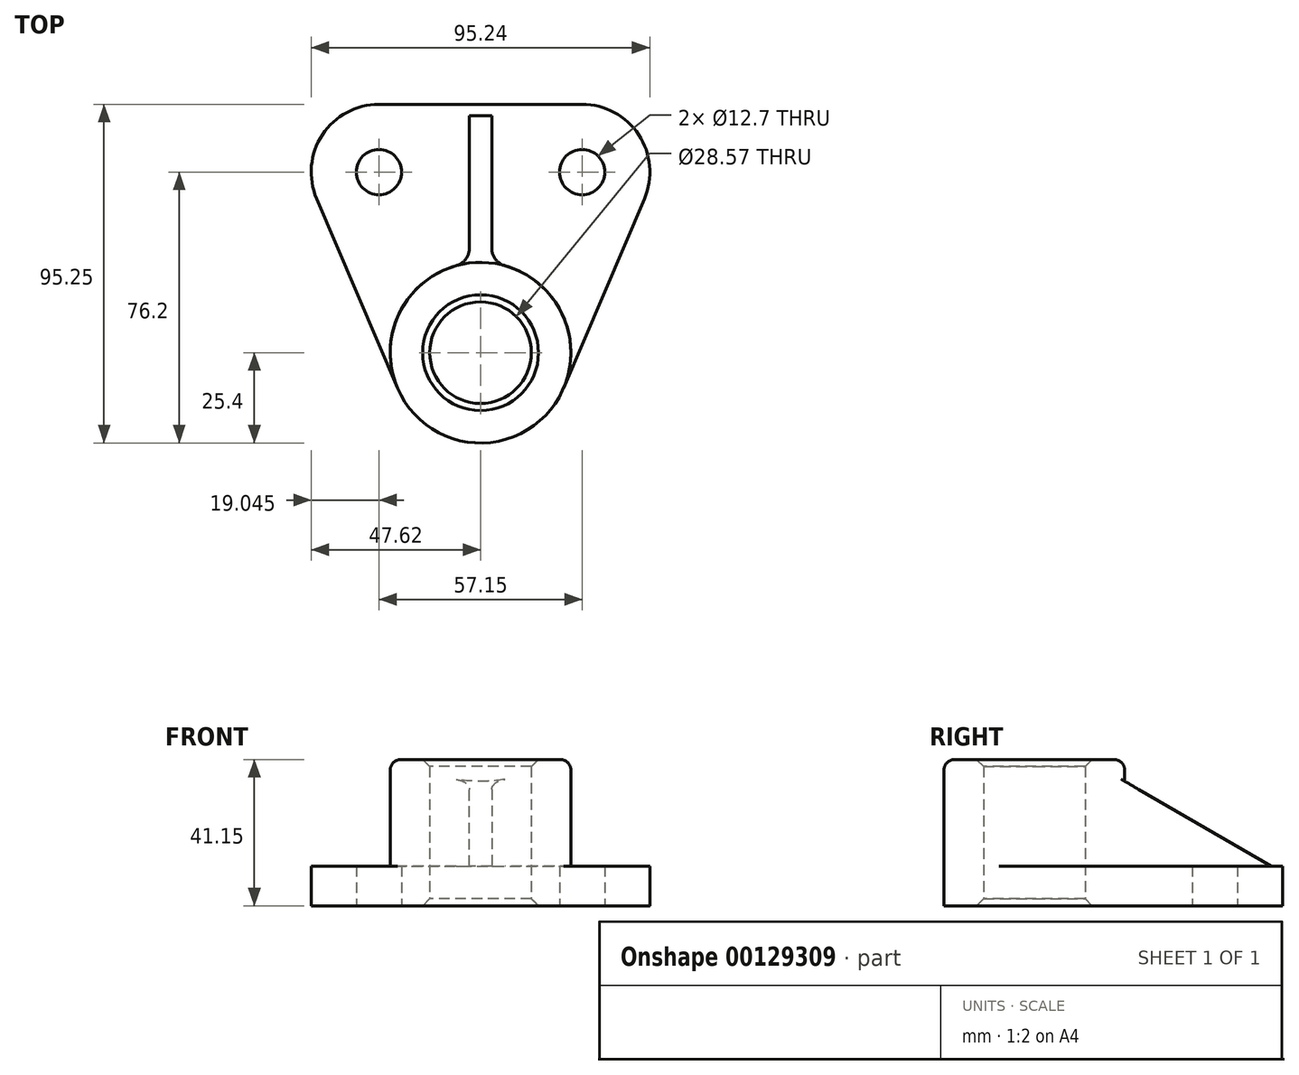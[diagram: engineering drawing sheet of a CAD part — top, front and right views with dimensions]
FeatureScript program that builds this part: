
annotation { "Feature Type Name" : "Feature", "Feature Type Description" : "" }
export const myFeature = defineFeature(function(context is Context, id is Id, definition is map)
    precondition{}
    {
        {
            var Q0;
            Q0=qCreatedBy(makeId("Top.planeOp"),FACE);
            var sketch = newSketch(context, id + "F0", { "sketchPlane" : qUnion([Q0])});
            skCircle(sketch, "E0", {"center": v(0, 0) * mm, "radius": 25.4 * mm});
            skLineSegment(sketch, "E1", {"start": v(0, 0) * mm, "end": v(0, 69.85) * mm, "construction": true});
            skLineSegment(sketch, "E2", {"start": v(-23.36, -9.97) * mm, "end": v(-46.1, 43.33) * mm});
            skArc(sketch, "E3.filletArc", {"start": v(-28.58, 69.85) * mm, "mid": v(-44.47, 61.3) * mm, "end": v(-46.1, 43.33) * mm});
            skCircle(sketch, "E4", {"center": v(0, 0) * mm, "radius": 14.29 * mm});
            skCircle(sketch, "E5", {"center": v(-28.58, 50.8) * mm, "radius": 6.35 * mm});
            skArc(sketch, "E6.0.MirrorCS", {"start": v(28.58, 69.85) * mm, "mid": v(44.47, 61.3) * mm, "end": v(46.1, 43.33) * mm});
            skLineSegment(sketch, "E7.0.MirrorCS", {"start": v(23.36, -9.97) * mm, "end": v(46.1, 43.33) * mm});
            skCircle(sketch, "E8.0.MirrorC", {"center": v(28.58, 50.8) * mm, "radius": 6.35 * mm});
            skLineSegment(sketch, "E9", {"start": v(-28.58, 69.85) * mm, "end": v(28.58, 69.85) * mm});
            skSolve(sketch);
        }
        {
            var Q0;
            Q0=makeQuery(id+"F0.imprint","IMPRINT",FACE,{"disambiguationData":[TD([[makeQuery(id+"F0.imprint","IMPRINT",EDGE,{"derivedFrom":sQuery(id+"F0.wireOp",EDGE,"E4")}),-1.0]])]});
            extrude(context, id + "F1", {"entities" : qUnion([Q0]), "depth" : 41.15 * mm});
        }
        {
            var Q0;
            {var subQ1=sQuery(id+"F0.wireOp",EDGE,"E2");Q0=makeQuery(id+"F0.imprint","IMPRINT",FACE,{"disambiguationData":[TD([[makeQuery(id+"F0.imprint","IMPRINT",EDGE,{"derivedFrom":subQ1}),-1.0]])]});}
            extrude(context, id + "F2", {"entities" : qUnion([Q0]), "operationType" : NewBodyOperationType.ADD, "depth" : 11.18 * mm});
        }
        {
            var Q0;
            Q0=qCreatedBy(makeId("Right.planeOp"),FACE);
            var sketch = newSketch(context, id + "F3", { "sketchPlane" : qUnion([Q0])});
            skLineSegment(sketch, "E10", {"start": v(-25.4, 0) * mm, "end": v(-25.4, 41.15) * mm});
            skLineSegment(sketch, "E11", {"start": v(25.4, 41.97) * mm, "end": v(25.4, 11.18) * mm});
            skLineSegment(sketch, "E12.0", {"start": v(22.23, 41.97) * mm, "end": v(22.23, 11.18) * mm});
            skLineSegment(sketch, "E13", {"start": v(22.23, 36.84) * mm, "end": v(66.67, 11.18) * mm});
            skLineSegment(sketch, "E14", {"start": v(66.67, 11.18) * mm, "end": v(22.23, 11.18) * mm});
            skLineSegment(sketch, "E15", {"start": v(22.22, 11.18) * mm, "end": v(22.23, 36.84) * mm});
            skSolve(sketch);
        }
        {
            var Q0;
            Q0=qSketchRegion(id+"F3",true);
            extrude(context, id + "F4", {"entities" : qUnion([Q0]), "operationType" : NewBodyOperationType.ADD, "endBound" : BoundingType.SYMMETRIC, "depth" : 6.35 * mm});
        }
        {
            var Q0;
            {var subQ0=sQuery(id+"F0.wireOp",EDGE,"E0");var subQ1=sQuery(id+"F0.wireOp",EDGE,"E7.0.MirrorCS");Q0=makeQuery(id+"F4.boolean.opBoolean","SPLIT",EDGE,{"disambiguationData":[TD([makeQuery(id+"F2.opExtrude","SWEPT_FACE",FACE,{"disambiguationData":[OSD([subQ1])]})])],"derivedFrom":makeQuery(id+"F2.opExtrude","CAP_EDGE",EDGE,{"disambiguationData":[OSD([subQ0])],"isStart":false})});}
            var Q1;
            Q1=makeQuery(id+"F4.opExtrude","CAP_EDGE",EDGE,{"disambiguationData":[OSD([sQuery(id+"F3.wireOp",EDGE,"E14")])],"isStart":false});
            var Q2;
            Q2=makeQuery(id+"F4.boolean.opBoolean","INTERSECT",EDGE,{"derivedFrom":[makeQuery(id+"F1.opExtrude","SWEPT_FACE",FACE,{"disambiguationData":[OSD([sQuery(id+"F0.wireOp",EDGE,"E0")])]}),makeQuery(id+"F4.opExtrude","CAP_FACE",FACE,{"disambiguationData":[OSD([sQuery(id+"F3.wireOp",EDGE,"E13"),sQuery(id+"F3.wireOp",EDGE,"E14"),sQuery(id+"F3.wireOp",EDGE,"E15")])],"isStart":false})]});
            var Q3;
            Q3=makeQuery(id+"F4.boolean.opBoolean","INTERSECT",EDGE,{"derivedFrom":[makeQuery(id+"F1.opExtrude","SWEPT_FACE",FACE,{"disambiguationData":[OSD([sQuery(id+"F0.wireOp",EDGE,"E0")])]}),makeQuery(id+"F4.opExtrude","CAP_FACE",FACE,{"disambiguationData":[OSD([sQuery(id+"F3.wireOp",EDGE,"E13"),sQuery(id+"F3.wireOp",EDGE,"E14"),sQuery(id+"F3.wireOp",EDGE,"E15")])],"isStart":true})]});
            var Q4;
            Q4=makeQuery(id+"F4.opExtrude","CAP_EDGE",EDGE,{"disambiguationData":[OSD([sQuery(id+"F3.wireOp",EDGE,"E14")])],"isStart":true});
            var Q5;
            {var subQ0=sQuery(id+"F0.wireOp",EDGE,"E0");var subQ1=sQuery(id+"F0.wireOp",EDGE,"E2");Q5=makeQuery(id+"F4.boolean.opBoolean","SPLIT",EDGE,{"disambiguationData":[TD([makeQuery(id+"F2.opExtrude","SWEPT_FACE",FACE,{"disambiguationData":[OSD([subQ1])]})])],"derivedFrom":makeQuery(id+"F2.opExtrude","CAP_EDGE",EDGE,{"disambiguationData":[OSD([subQ0])],"isStart":false})});}
            fillet(context, id + "F5", {"entities" : qUnion([Q0, Q1, Q2, Q3, Q4, Q5]), "radius" : 5 * mm, "tangentPropagation" : true, "allowEdgeOverflow" : false});
        }
        {
            var Q0;
            Q0=makeQuery(id+"F1.opExtrude","CAP_EDGE",EDGE,{"disambiguationData":[OSD([sQuery(id+"F0.wireOp",EDGE,"E4")])],"isStart":true});
            var Q1;
            Q1=makeQuery(id+"F1.opExtrude","CAP_EDGE",EDGE,{"disambiguationData":[OSD([sQuery(id+"F0.wireOp",EDGE,"E4")])],"isStart":false});
            chamfer(context, id + "F6", {"entities" : qUnion([Q0, Q1]), "width" : 2 * mm, "tangentPropagation" : true});
        }
        {
            var Q0;
            Q0=makeQuery(id+"F1.opExtrude","CAP_EDGE",EDGE,{"disambiguationData":[OSD([sQuery(id+"F0.wireOp",EDGE,"E0")])],"isStart":false});
            fillet(context, id + "F7", {"entities" : qUnion([Q0]), "radius" : 3 * mm, "tangentPropagation" : true, "allowEdgeOverflow" : false});
        }
    });
